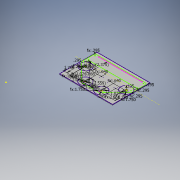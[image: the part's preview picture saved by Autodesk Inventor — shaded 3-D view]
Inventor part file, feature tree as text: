
AUTODESK INVENTOR PART (.ipt)
format: ipt  version: 2016 (Build 200138000, 138)  size: 212,992 bytes
history: native  units: in
note: dims shown in document units (in); Inventor stores cm internally (conversion verified against a paired STEP export)
features: sketch x7, extrude x4, hole x2
ambient origin geometry x8: Origin, YZ Plane, XZ Plane, XY Plane, X Axis, Y Axis, Z Axis, Center Point
bodies: Solid1 (feature_tree)
feature tree (13):
  extrude  "Extrusion1"  Depth=6.0in
  hole  "Hole1"  [1 undecoded]
  extrude  "Extrusion3"  Depth=3.1102in
  hole  "Hole2"  [1 undecoded]
  extrude  "Extrusion4"  Depth=1.0236in
  extrude  "Extrusion5"  Depth=7.5728in
  sketch  "Sketch9"  dims[d24=0.2953in d32=0.2953in d33=0.2953in d36=0.5in d40=3.8881in d43=1.0in d44=0.0in d45=1.75in d47=1.75in d48=1.75in d49=1.75in d50=2.25in d52=2.5591in d53=0.6398in d54=0.6398in d55=2.25in d56=1.75in d58=2.0472in d59=1.0236in d60=1.75in d61=1.0236in d62=1.2795in d63=0.4in d64=0.1181in d65=0.75in d66=0.375in d67=0.25in d68=0.5635in d69=1.0in d70=0.8108in d72=0.2362in d76=0.236in d77=0.492in d78=0.236in d79=0.492in d80=1.0in d81=0.0in d82=0.236in d83=0.492in d84=0.236in d85=0.492in d86=1.0in d87=0.0in d88=0.2362in d90=0.125in d91=0.125in d93=0.2953in d95=2.3746in d96=2.07in d98=0.4625in d99=0.295in d101=0.4625in d102=0.295in d103=0.2953in d104=0.2953in d106=0.2362in]
  sketch  "Sketch1"  dims[d0=8.5in d1=6.0in]
  sketch  "Sketch2"  dims[d2=0.125in d3=0.0in d4=5.6831in]
  sketch  "Sketch3"  dims[d5=1.0236in d7=3.1102in]
  sketch  "Sketch5"  dims[d12=0.2362in d13=0.75in d14=0.375in d15=0.25in d16=0.5635in d17=1.0in d18=0.8108in d19=1.0768in]
  sketch  "Sketch7"  dims[d20=3.1102in d21=1.0236in]
  sketch  "Sketch8"  dims[d22=3.124in d23=7.5728in]
note: 2 required parameter values undecoded (feature->parameter linkage not recoverable at this tier; creation-order binding heuristic only, values carry confidence <= 0.55)
